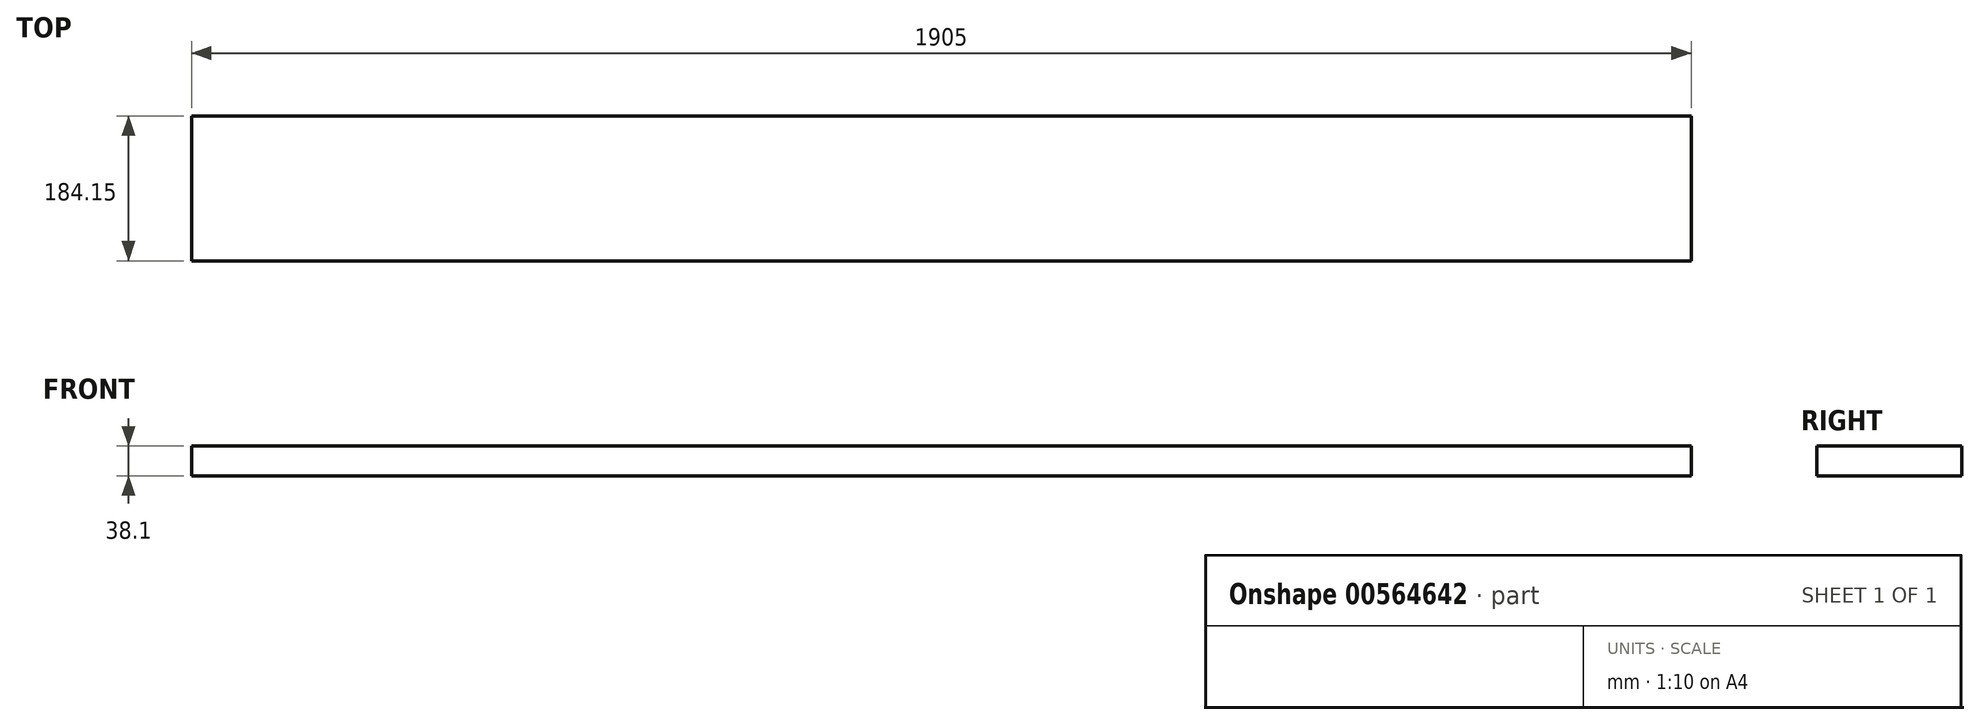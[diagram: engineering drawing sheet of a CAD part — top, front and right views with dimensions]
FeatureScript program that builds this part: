
annotation { "Feature Type Name" : "Feature", "Feature Type Description" : "" }
export const myFeature = defineFeature(function(context is Context, id is Id, definition is map)
    precondition{}
    {
        {
            var Q0;
            Q0=qCreatedBy(makeId("Top.planeOp"),FACE);
            var sketch = newSketch(context, id + "F0", { "sketchPlane" : qUnion([Q0])});
            skLineSegment(sketch, "E0.bottom", {"start": v(0, 0) * mm, "end": v(1905, 0) * mm});
            skLineSegment(sketch, "E0.top", {"start": v(0, 184.15) * mm, "end": v(1905, 184.15) * mm});
            skLineSegment(sketch, "E0.left", {"start": v(0, 0) * mm, "end": v(0, 184.15) * mm});
            skLineSegment(sketch, "E0.right", {"start": v(1905, 0) * mm, "end": v(1905, 184.15) * mm});
            skSolve(sketch);
        }
        {
            var Q0;
            Q0=makeQuery(id+"F0.imprint","IMPRINT",FACE,{"disambiguationData":[TD([[makeQuery(id+"F0.imprint","IMPRINT",EDGE,{"derivedFrom":sQuery(id+"F0.wireOp",EDGE,"E0.bottom")}),1.0]])]});
            extrude(context, id + "F1", {"entities" : qUnion([Q0]), "depth" : 38.1 * mm, "offsetDistance" : 25.4 * mm});
        }
    });
